# Revit family: E_Cable Tray Support_MEPcontent_OBO Bettermann_Bracket
name_source: partatom
category: Cable Tray Fittings
revit_build: Autodesk Revit MEP 2015 (Build: 20140606_1530(x64)
units: mm (PartAtom-declared; Revit-internal decimal feet)

## types (3) — shared parameters
Depth = 30 mm  [stored 0.0984252 ft]
EMCS Version = 2.0
ETIM Article Class = EC001003
Family Version = 10.14
Gray = Color RGB 189-187-185
Height = 180 mm
Height 1 = 180 mm  [stored 0.590551 ft]
IFCExportAs = IfcCableCarrierFittingType
IFCExportType = NOTDEFINED
MEPcontent Class = CABLE_TRAY_SUPPORT
Manufacturer = OBO BETTERMANN
Manufacturer URL = http://catalog4.obo-bettermann.com
Product Line = OBO BETTERMANN
Revit Version = 2015
URL = www.stabiplan.com

## per-type parameters (varying)
| type | Article Description | Description | GTIN | Manufacturer Art. No. | Width | Width 1 |
| AHB 100 FT | Cable Tray Bracket | Cable Tray Bracket | 4012196881413 | 6363903 | 100 mm | 100 mm  [stored 0.328084 ft] |
| AHB 200 FT | Horizontal CableTray Bracket | Horizontal CableTray Bracket | 4012196881475 | 6363911 | 200 mm | 200 mm  [stored 0.656168 ft] |
| AHB 300 FT | Cable Tray Bracket | Cable Tray Bracket | 4012196881536 | 6363938 | 300 mm | 300 mm |

note: column(s) folded — value = type name in every type: Article Type, Model

note: [stored X ft] marks values corroborated as IEEE doubles in the binary element streams (Revit-internal decimal feet)

## geometry (parser evidence)
native form markers: Blend x4, Sweep x2
no freeform markers — native parametric forms only
